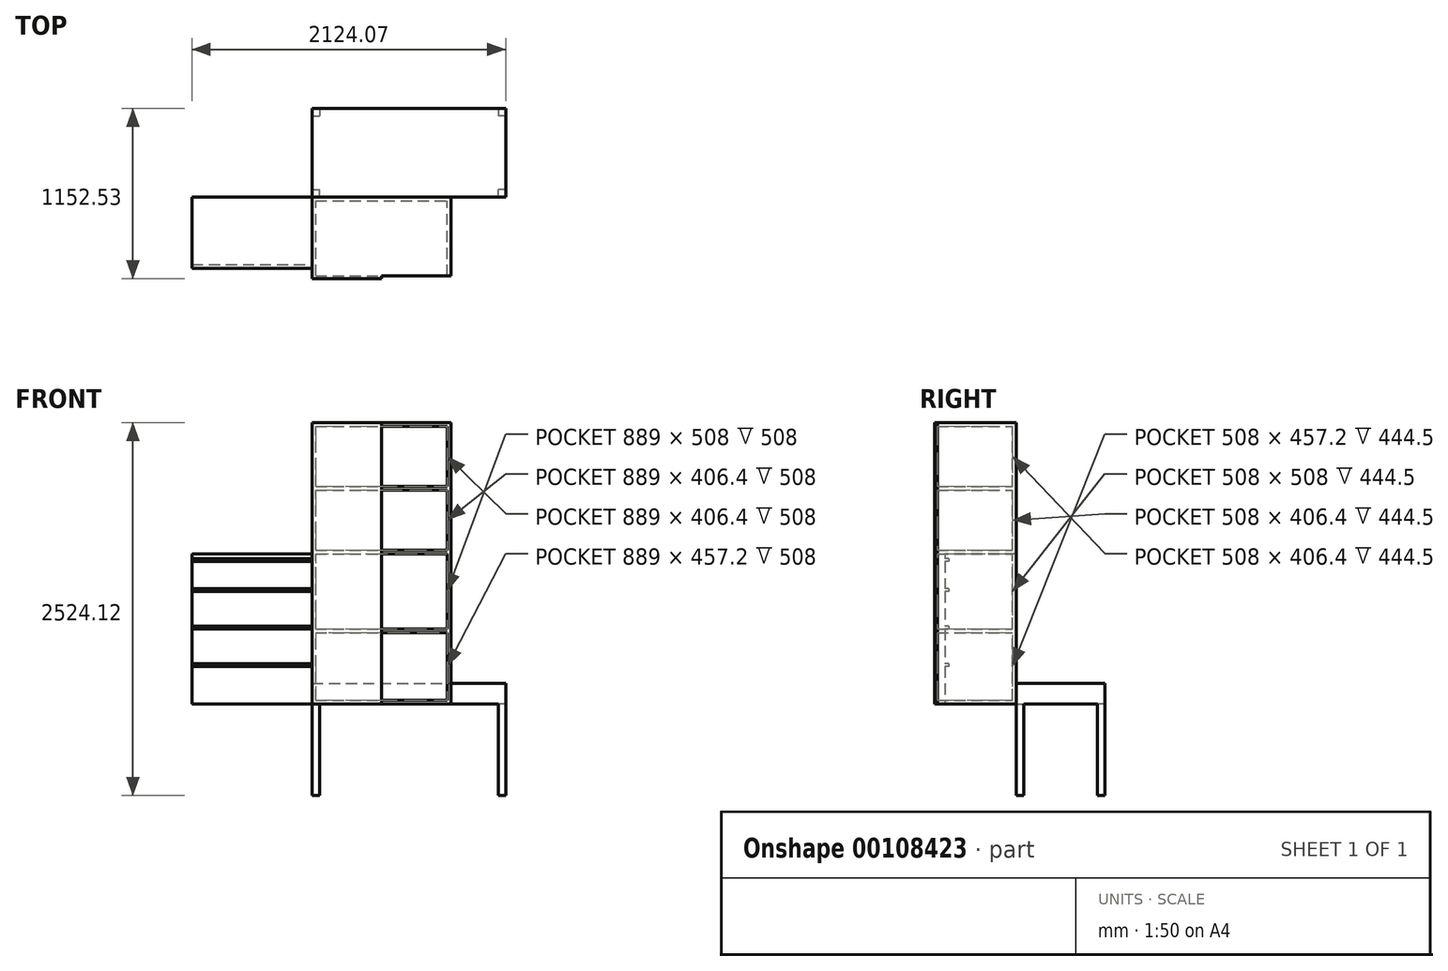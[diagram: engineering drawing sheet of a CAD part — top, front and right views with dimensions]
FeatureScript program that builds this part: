
annotation { "Feature Type Name" : "Feature", "Feature Type Description" : "" }
export const myFeature = defineFeature(function(context is Context, id is Id, definition is map)
    precondition{}
    {
        {
            var Q0;
            Q0=qCreatedBy(makeId("Front.planeOp"),FACE);
            var sketch = newSketch(context, id + "F0", { "sketchPlane" : qUnion([Q0])});
            skLineSegment(sketch, "E0.bottom", {"start": v(0, 0) * mm, "end": v(939.8, 0) * mm});
            skLineSegment(sketch, "E0.top", {"start": v(0, 1905) * mm, "end": v(939.8, 1905) * mm});
            skLineSegment(sketch, "E0.left", {"start": v(0, 0) * mm, "end": v(0, 1905) * mm});
            skLineSegment(sketch, "E0.right", {"start": v(939.8, 0) * mm, "end": v(939.8, 1905) * mm});
            skSolve(sketch);
        }
        {
            var Q0;
            Q0=qSketchRegion(id+"F0",true);
            extrude(context, id + "F1", {"entities" : qUnion([Q0]), "depth" : 25.4 * mm});
        }
        {
            var Q0;
            Q0=makeQuery(id+"F1.opExtrude","CAP_FACE",FACE,{"disambiguationData":[OSD([sQuery(id+"F0.wireOp",EDGE,"E0.bottom"),sQuery(id+"F0.wireOp",EDGE,"E0.top"),sQuery(id+"F0.wireOp",EDGE,"E0.left"),sQuery(id+"F0.wireOp",EDGE,"E0.right")])],"isStart":false});
            var sketch = newSketch(context, id + "F2", { "sketchPlane" : qUnion([Q0])});
            skLineSegment(sketch, "E1.0", {"start": v(0, 1905) * mm, "end": v(939.8, 1905) * mm});
            skLineSegment(sketch, "E2.0", {"start": v(939.8, 0) * mm, "end": v(939.8, 1905) * mm});
            skLineSegment(sketch, "E3.0", {"start": v(0, 0) * mm, "end": v(939.8, 0) * mm});
            skLineSegment(sketch, "E4.0", {"start": v(0, 0) * mm, "end": v(0, 1905) * mm});
            skLineSegment(sketch, "E5.0", {"start": v(25.4, 1879.6) * mm, "end": v(914.4, 1879.6) * mm});
            skLineSegment(sketch, "E6.0", {"start": v(914.4, 25.4) * mm, "end": v(914.4, 1879.6) * mm});
            skLineSegment(sketch, "E7.0", {"start": v(25.4, 25.4) * mm, "end": v(914.4, 25.4) * mm});
            skLineSegment(sketch, "E8.0", {"start": v(25.4, 25.4) * mm, "end": v(25.4, 1879.6) * mm});
            skSolve(sketch);
        }
        {
            var Q0;
            Q0=qSketchRegion(id+"F2",true);
            extrude(context, id + "F3", {"entities" : qUnion([Q0]), "operationType" : NewBodyOperationType.ADD, "depth" : 508 * mm});
        }
        {
            var Q0;
            Q0=makeQuery(id+"F3.opExtrude","CAP_FACE",FACE,{"disambiguationData":[OSD([sQuery(id+"F2.wireOp",EDGE,"E1.0"),sQuery(id+"F2.wireOp",EDGE,"E2.0"),sQuery(id+"F2.wireOp",EDGE,"E3.0"),sQuery(id+"F2.wireOp",EDGE,"E4.0"),sQuery(id+"F2.wireOp",EDGE,"E5.0"),sQuery(id+"F2.wireOp",EDGE,"E6.0"),sQuery(id+"F2.wireOp",EDGE,"E7.0"),sQuery(id+"F2.wireOp",EDGE,"E8.0")])],"isStart":false});
            var sketch = newSketch(context, id + "F4", { "sketchPlane" : qUnion([Q0])});
            skLineSegment(sketch, "E9.bottom", {"start": v(0, 0) * mm, "end": v(469.9, 0) * mm});
            skLineSegment(sketch, "E9.top", {"start": v(0, 1905) * mm, "end": v(469.9, 1905) * mm});
            skLineSegment(sketch, "E9.left", {"start": v(0, 0) * mm, "end": v(0, 1905) * mm});
            skLineSegment(sketch, "E9.right", {"start": v(469.9, 0) * mm, "end": v(469.9, 1905) * mm});
            skSolve(sketch);
        }
        {
            var Q0;
            Q0=qSketchRegion(id+"F4",true);
            extrude(context, id + "F5", {"entities" : qUnion([Q0]), "depth" : 19.05 * mm});
        }
        {
            var Q0;
            Q0=qCreatedBy(makeId("Top.planeOp"),FACE);
            var sketch = newSketch(context, id + "F6", { "sketchPlane" : qUnion([Q0])});
            skLineSegment(sketch, "E10.bottom", {"start": v(0, 0) * mm, "end": v(1311.28, 0) * mm});
            skLineSegment(sketch, "E10.top", {"start": v(0, 600.07) * mm, "end": v(1311.27, 600.07) * mm});
            skLineSegment(sketch, "E10.left", {"start": v(0, 0) * mm, "end": v(0, 600.07) * mm});
            skLineSegment(sketch, "E10.right", {"start": v(1311.28, 0) * mm, "end": v(1311.28, 600.07) * mm});
            skSolve(sketch);
        }
        {
            var Q0;
            Q0=qSketchRegion(id+"F6",true);
            extrude(context, id + "F7", {"entities" : qUnion([Q0]), "depth" : 139.7 * mm});
        }
        {
            var Q0;
            Q0=makeQuery(id+"F7.opExtrude","CAP_FACE",FACE,{"disambiguationData":[OSD([sQuery(id+"F6.wireOp",EDGE,"E10.bottom"),sQuery(id+"F6.wireOp",EDGE,"E10.top"),sQuery(id+"F6.wireOp",EDGE,"E10.left"),sQuery(id+"F6.wireOp",EDGE,"E10.right")])],"isStart":true});
            var sketch = newSketch(context, id + "F8", { "sketchPlane" : qUnion([Q0])});
            skLineSegment(sketch, "E11.bottom", {"start": v(0, 0) * mm, "end": v(50.8, 0) * mm});
            skLineSegment(sketch, "E11.top", {"start": v(0, -50.8) * mm, "end": v(50.8, -50.8) * mm});
            skLineSegment(sketch, "E11.left", {"start": v(0, 0) * mm, "end": v(0, -50.8) * mm});
            skLineSegment(sketch, "E11.right", {"start": v(50.8, 0) * mm, "end": v(50.8, -50.8) * mm});
            skLineSegment(sketch, "E12.bottom", {"start": v(0, -600.07) * mm, "end": v(50.8, -600.07) * mm});
            skLineSegment(sketch, "E12.top", {"start": v(0, -549.28) * mm, "end": v(50.8, -549.28) * mm});
            skLineSegment(sketch, "E12.left", {"start": v(0, -600.07) * mm, "end": v(0, -549.28) * mm});
            skLineSegment(sketch, "E12.right", {"start": v(50.8, -600.07) * mm, "end": v(50.8, -549.28) * mm});
            skLineSegment(sketch, "E13.bottom", {"start": v(1311.28, -600.07) * mm, "end": v(1260.48, -600.07) * mm});
            skLineSegment(sketch, "E13.top", {"start": v(1311.28, -549.28) * mm, "end": v(1260.48, -549.28) * mm});
            skLineSegment(sketch, "E13.left", {"start": v(1311.28, -600.07) * mm, "end": v(1311.28, -549.28) * mm});
            skLineSegment(sketch, "E13.right", {"start": v(1260.48, -600.07) * mm, "end": v(1260.48, -549.28) * mm});
            skLineSegment(sketch, "E14.bottom", {"start": v(1311.28, 0) * mm, "end": v(1260.48, 0) * mm});
            skLineSegment(sketch, "E14.top", {"start": v(1311.28, -50.8) * mm, "end": v(1260.48, -50.8) * mm});
            skLineSegment(sketch, "E14.left", {"start": v(1311.28, 0) * mm, "end": v(1311.28, -50.8) * mm});
            skLineSegment(sketch, "E14.right", {"start": v(1260.48, 0) * mm, "end": v(1260.48, -50.8) * mm});
            skSolve(sketch);
        }
        {
            var Q0;
            Q0=qSketchRegion(id+"F8",true);
            extrude(context, id + "F9", {"entities" : qUnion([Q0]), "operationType" : NewBodyOperationType.ADD, "depth" : 619.12 * mm});
        }
        {
            var Q0;
            Q0=makeQuery(id+"F1.opExtrude","CAP_FACE",FACE,{"disambiguationData":[OSD([sQuery(id+"F0.wireOp",EDGE,"E0.bottom"),sQuery(id+"F0.wireOp",EDGE,"E0.top"),sQuery(id+"F0.wireOp",EDGE,"E0.left"),sQuery(id+"F0.wireOp",EDGE,"E0.right")])],"isStart":false});
            var sketch = newSketch(context, id + "F10", { "sketchPlane" : qUnion([Q0])});
            skLineSegment(sketch, "E15.bottom", {"start": v(25.4, 482.6) * mm, "end": v(914.4, 482.6) * mm});
            skLineSegment(sketch, "E15.top", {"start": v(25.4, 508) * mm, "end": v(914.4, 508) * mm});
            skLineSegment(sketch, "E15.left", {"start": v(25.4, 482.6) * mm, "end": v(25.4, 508) * mm});
            skLineSegment(sketch, "E15.right", {"start": v(914.4, 482.6) * mm, "end": v(914.4, 508) * mm});
            skLineSegment(sketch, "E16.bottom", {"start": v(25.4, 1016) * mm, "end": v(914.4, 1016) * mm});
            skLineSegment(sketch, "E16.top", {"start": v(25.4, 1041.4) * mm, "end": v(914.4, 1041.4) * mm});
            skLineSegment(sketch, "E16.left", {"start": v(25.4, 1016) * mm, "end": v(25.4, 1041.4) * mm});
            skLineSegment(sketch, "E16.right", {"start": v(914.4, 1016) * mm, "end": v(914.4, 1041.4) * mm});
            skLineSegment(sketch, "E17.bottom", {"start": v(25.4, 1447.8) * mm, "end": v(914.4, 1447.8) * mm});
            skLineSegment(sketch, "E17.top", {"start": v(25.4, 1473.2) * mm, "end": v(914.4, 1473.2) * mm});
            skLineSegment(sketch, "E17.left", {"start": v(25.4, 1447.8) * mm, "end": v(25.4, 1473.2) * mm});
            skLineSegment(sketch, "E17.right", {"start": v(914.4, 1447.8) * mm, "end": v(914.4, 1473.2) * mm});
            skSolve(sketch);
        }
        {
            var Q0;
            Q0=qSketchRegion(id+"F10",true);
            var Q1;
            Q1=makeQuery(id+"F3.opExtrude","CAP_FACE",FACE,{"disambiguationData":[OSD([sQuery(id+"F2.wireOp",EDGE,"E1.0"),sQuery(id+"F2.wireOp",EDGE,"E2.0"),sQuery(id+"F2.wireOp",EDGE,"E3.0"),sQuery(id+"F2.wireOp",EDGE,"E4.0"),sQuery(id+"F2.wireOp",EDGE,"E5.0"),sQuery(id+"F2.wireOp",EDGE,"E6.0"),sQuery(id+"F2.wireOp",EDGE,"E7.0"),sQuery(id+"F2.wireOp",EDGE,"E8.0")])],"isStart":false});
            extrude(context, id + "F11", {"entities" : qUnion([Q0]), "operationType" : NewBodyOperationType.ADD, "endBound" : BoundingType.UP_TO_SURFACE, "endBoundEntityFace" : qUnion([Q1]), "depth" : 25.4 * mm});
        }
        {
            var Q0;
            Q0=qCreatedBy(makeId("Top.planeOp"),FACE);
            var sketch = newSketch(context, id + "F12", { "sketchPlane" : qUnion([Q0])});
            skLineSegment(sketch, "E18.bottom", {"start": v(0, 0) * mm, "end": v(-812.8, 0) * mm});
            skLineSegment(sketch, "E18.top", {"start": v(0, -482.6) * mm, "end": v(-812.8, -482.6) * mm});
            skLineSegment(sketch, "E18.left", {"start": v(0, 0) * mm, "end": v(0, -482.6) * mm});
            skLineSegment(sketch, "E18.right", {"start": v(-812.8, 0) * mm, "end": v(-812.8, -482.6) * mm});
            skSolve(sketch);
        }
        {
            var Q0;
            Q0=qSketchRegion(id+"F12",true);
            extrude(context, id + "F13", {"entities" : qUnion([Q0]), "depth" : 1016 * mm});
        }
        {
            var Q0;
            Q0=makeQuery(id+"F13.opExtrude","SWEPT_FACE",FACE,{"disambiguationData":[OSD([sQuery(id+"F12.wireOp",EDGE,"E18.top")])]});
            var sketch = newSketch(context, id + "F14", { "sketchPlane" : qUnion([Q0])});
            skLineSegment(sketch, "E19.bottom", {"start": v(-812.8, 984.25) * mm, "end": v(0, 984.25) * mm});
            skLineSegment(sketch, "E19.top", {"start": v(-812.8, 965.2) * mm, "end": v(0, 965.2) * mm});
            skLineSegment(sketch, "E19.left", {"start": v(-812.8, 984.25) * mm, "end": v(-812.8, 965.2) * mm});
            skLineSegment(sketch, "E19.right", {"start": v(0, 984.25) * mm, "end": v(0, 965.2) * mm});
            skLineSegment(sketch, "E20.bottom", {"start": v(-812.8, 781.05) * mm, "end": v(0, 781.05) * mm});
            skLineSegment(sketch, "E20.top", {"start": v(-812.8, 762) * mm, "end": v(0, 762) * mm});
            skLineSegment(sketch, "E20.left", {"start": v(-812.8, 781.05) * mm, "end": v(-812.8, 762) * mm});
            skLineSegment(sketch, "E20.right", {"start": v(0, 781.05) * mm, "end": v(0, 762) * mm});
            skLineSegment(sketch, "E21.bottom", {"start": v(-812.8, 527.05) * mm, "end": v(0, 527.05) * mm});
            skLineSegment(sketch, "E21.top", {"start": v(-812.8, 508) * mm, "end": v(0, 508) * mm});
            skLineSegment(sketch, "E21.left", {"start": v(-812.8, 527.05) * mm, "end": v(-812.8, 508) * mm});
            skLineSegment(sketch, "E21.right", {"start": v(0, 527.05) * mm, "end": v(0, 508) * mm});
            skLineSegment(sketch, "E22.bottom", {"start": v(-812.8, 273.05) * mm, "end": v(0, 273.05) * mm});
            skLineSegment(sketch, "E22.top", {"start": v(-812.8, 254) * mm, "end": v(0, 254) * mm});
            skLineSegment(sketch, "E22.left", {"start": v(-812.8, 273.05) * mm, "end": v(-812.8, 254) * mm});
            skLineSegment(sketch, "E22.right", {"start": v(0, 273.05) * mm, "end": v(0, 254) * mm});
            skSolve(sketch);
        }
        {
            var Q0;
            Q0=qSketchRegion(id+"F14",true);
            extrude(context, id + "F15", {"entities" : qUnion([Q0]), "operationType" : NewBodyOperationType.REMOVE, "oppositeDirection" : true, "depth" : 25.4 * mm});
        }
    });
